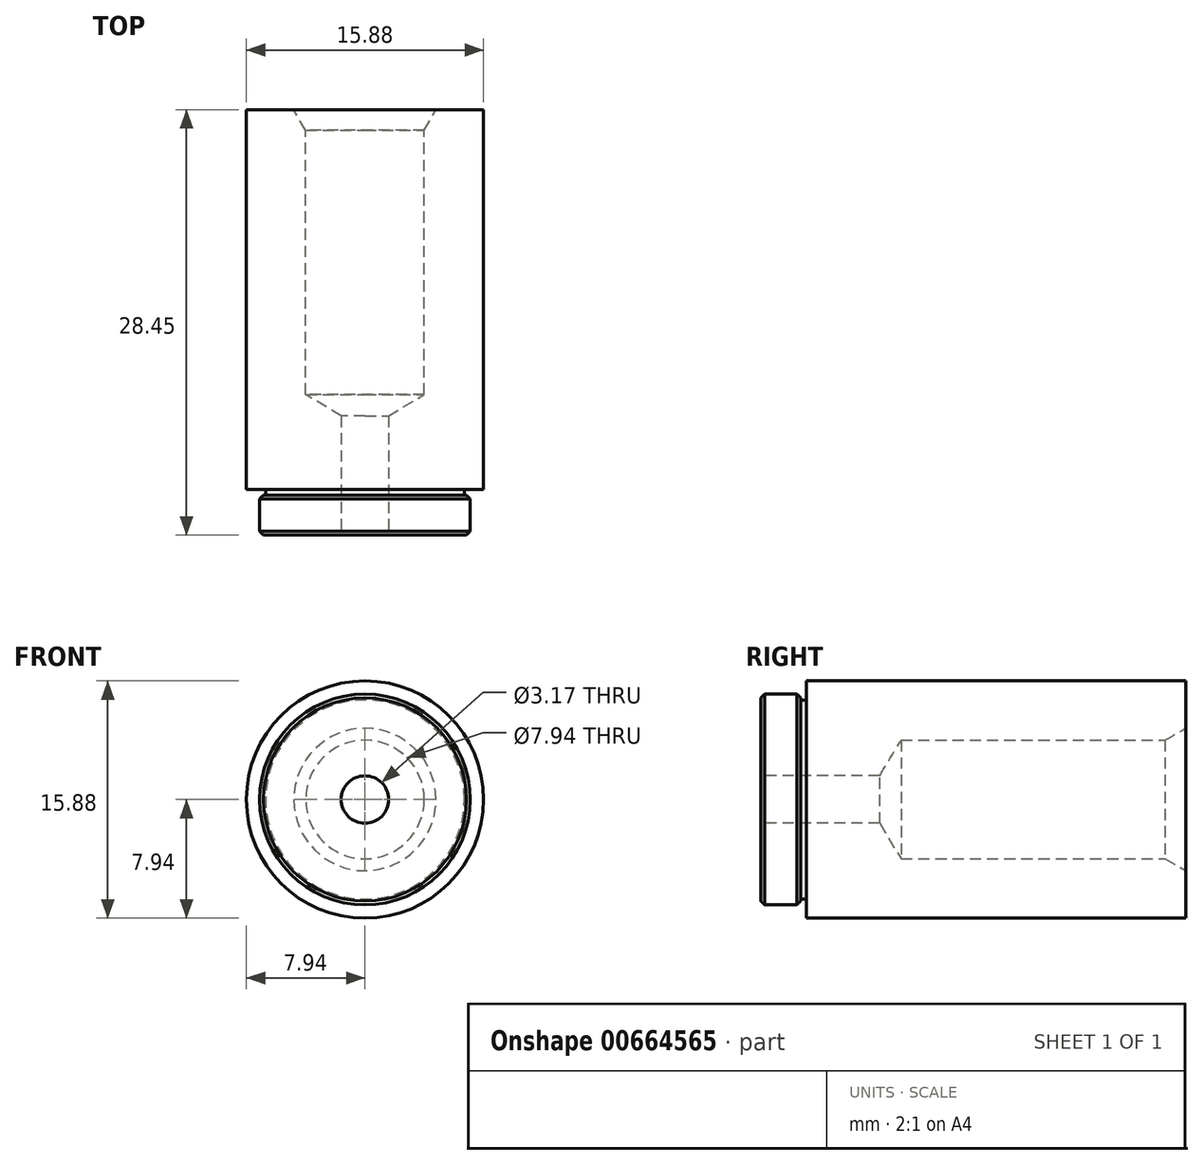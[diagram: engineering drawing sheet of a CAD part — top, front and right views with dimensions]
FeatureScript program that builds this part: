
annotation { "Feature Type Name" : "Feature", "Feature Type Description" : "" }
export const myFeature = defineFeature(function(context is Context, id is Id, definition is map)
    precondition{}
    {
        {
            var Q0;
            Q0=qCreatedBy(makeId("Front.planeOp"),FACE);
            var sketch = newSketch(context, id + "F0", { "sketchPlane" : qUnion([Q0])});
            skCircle(sketch, "E0", {"center": v(0, 0) * mm, "radius": 7.94 * mm});
            skCircle(sketch, "E1", {"center": v(0, 0) * mm, "radius": 1.59 * mm});
            skCircle(sketch, "E2", {"center": v(0, 0) * mm, "radius": 6.65 * mm});
            skSolve(sketch);
        }
        {
            var Q0;
            Q0 = qSketchRegion(id + "F0", true);
            var Q1;
            Q1=makeQuery(id+"F0.imprint","IMPRINT",FACE,{"disambiguationData":[TD([[makeQuery(id+"F0.imprint","IMPRINT",EDGE,{"derivedFrom":sQuery(id+"F0.wireOp",EDGE,"E1")}),-1.0]])]});
            extrude(context, id + "F1", {"entities" : qUnion([Q0, Q1]), "oppositeDirection" : true, "depth" : 25.4 * mm, "offsetDistance" : 25.4 * mm});
        }
        {
            var Q0;
            Q0=makeQuery(id+"F1.opExtrude","CAP_FACE",FACE,{"disambiguationData":[OSD([sQuery(id+"F0.wireOp",EDGE,"E0"),sQuery(id+"F0.wireOp",EDGE,"E1")])],"isStart":false});
            var sketch = newSketch(context, id + "F2", { "sketchPlane" : qUnion([Q0])});
            skPoint(sketch, "E3", {"position": v(0, 0) * mm});
            skSolve(sketch);
        }
        {
            var Q0;
            Q0=sQuery(id+"F2.wireOp",VERTEX,"E3");
            var Q1;
            Q1=makeQuery(id+"F1.opExtrude","SWEPT_BODY",BODY,{"disambiguationData":[OSD([sQuery(id+"F0.wireOp",EDGE,"E0"),sQuery(id+"F0.wireOp",EDGE,"E1")])]});
            hole(context, id + "F3", {"style" : HoleStyle.C_SINK, "endStyle" : HoleEndStyle.BLIND, "holeDiameter" : 7.94 * mm, "cSinkDiameter" : 9.52 * mm, "cSinkAngle" : 60 * degree, "majorDiameter" : 6.35 * mm, "holeDepth" : 19.05 * mm, "isTappedThrough" : true, "tappedDepth" : 6.35 * mm, "tapClearance" : 1, "locations" : qUnion([Q0]), "scope" : qUnion([Q1])});
        }
        {
            var Q0;
            Q0=makeQuery(id+"F0.imprint","IMPRINT",FACE,{"disambiguationData":[TD([[makeQuery(id+"F0.imprint","IMPRINT",EDGE,{"derivedFrom":sQuery(id+"F0.wireOp",EDGE,"E1")}),-1.0]])]});
            extrude(context, id + "F4", {"entities" : qUnion([Q0]), "operationType" : NewBodyOperationType.ADD, "depth" : 0.38 * mm, "offsetDistance" : 25.4 * mm});
        }
        {
            var Q0;
            Q0=makeQuery(id+"F4.opExtrude","CAP_FACE",FACE,{"disambiguationData":[OSD([sQuery(id+"F0.wireOp",EDGE,"E1"),sQuery(id+"F0.wireOp",EDGE,"E2")])],"isStart":false});
            var sketch = newSketch(context, id + "F5", { "sketchPlane" : qUnion([Q0])});
            skCircle(sketch, "E4", {"center": v(0, 0) * mm, "radius": 7.05 * mm});
            skCircle(sketch, "E5.0", {"center": v(0, 0) * mm, "radius": 1.59 * mm});
            skSolve(sketch);
        }
        {
            var Q0;
            Q0 = qSketchRegion(id + "F5", true);
            extrude(context, id + "F6", {"entities" : qUnion([Q0]), "operationType" : NewBodyOperationType.ADD, "depth" : 2.67 * mm, "offsetDistance" : 25.4 * mm});
        }
        {
            var Q0;
            Q0=makeQuery(id+"F6.opExtrude","CAP_EDGE",EDGE,{"disambiguationData":[OSD([sQuery(id+"F5.wireOp",EDGE,"E4")])],"isStart":false});
            var Q1;
            Q1=makeQuery(id+"F6.opExtrude","CAP_EDGE",EDGE,{"disambiguationData":[OSD([sQuery(id+"F5.wireOp",EDGE,"E4")])],"isStart":true});
            chamfer(context, id + "F7", {"entities" : qUnion([Q0, Q1]), "width" : 0.25 * mm, "tangentPropagation" : true});
        }
    });
